# Revit family: LTL
name_source: partatom
category: Lighting Fixtures
units: mm (PartAtom-declared; Revit-internal decimal feet)

## family parameters
Always vertical = Yes
Cut with Voids When Loaded = No
Host = Ceiling
Light Source = Yes
OmniClass Number = 23.80.70.11.14.11
OmniClass Title = Downlights
Part Type = Normal
Room Calculation Point = No
Round Connector Dimension = Use Diameter
Shared = No

## types (2) — shared parameters
Assembly Code = D5020200
Color Filter = 16777215
Description = LED Task Light luminaire
Dimming Lamp Color Temperature Shift = <None>
Housing Finish = Metal - Viscor - White
Lamp = LED
Lens Finish = Polycarbonate - Viscor - Frosted Round
Manufacturer = VISIONEERING by VISCOR
Model = LTL
Tilt Angle = 90.00°
URL = https://www.viscor.com
Voltage = 120 V
Width = 0' - 7"

## per-type parameters (varying)
| type | Apparent Load | Emit from Line Length | Lamp Wattage | Length | Photometric Web File |
| LTL48-LED840K030LUNV | 33 VA | 4' - 0" | 33 VA | 4' - 0" | LTL48-LED840K30LUNV.IES |
| LTL24-LED840K016LUUNV | 19 VA | 2' - 0" | 19 VA | 2' - 0" | LTL24-LED840K016LUNV.IES |

## geometry (parser evidence)
native form markers: Sweep x2
no freeform markers — native parametric forms only
